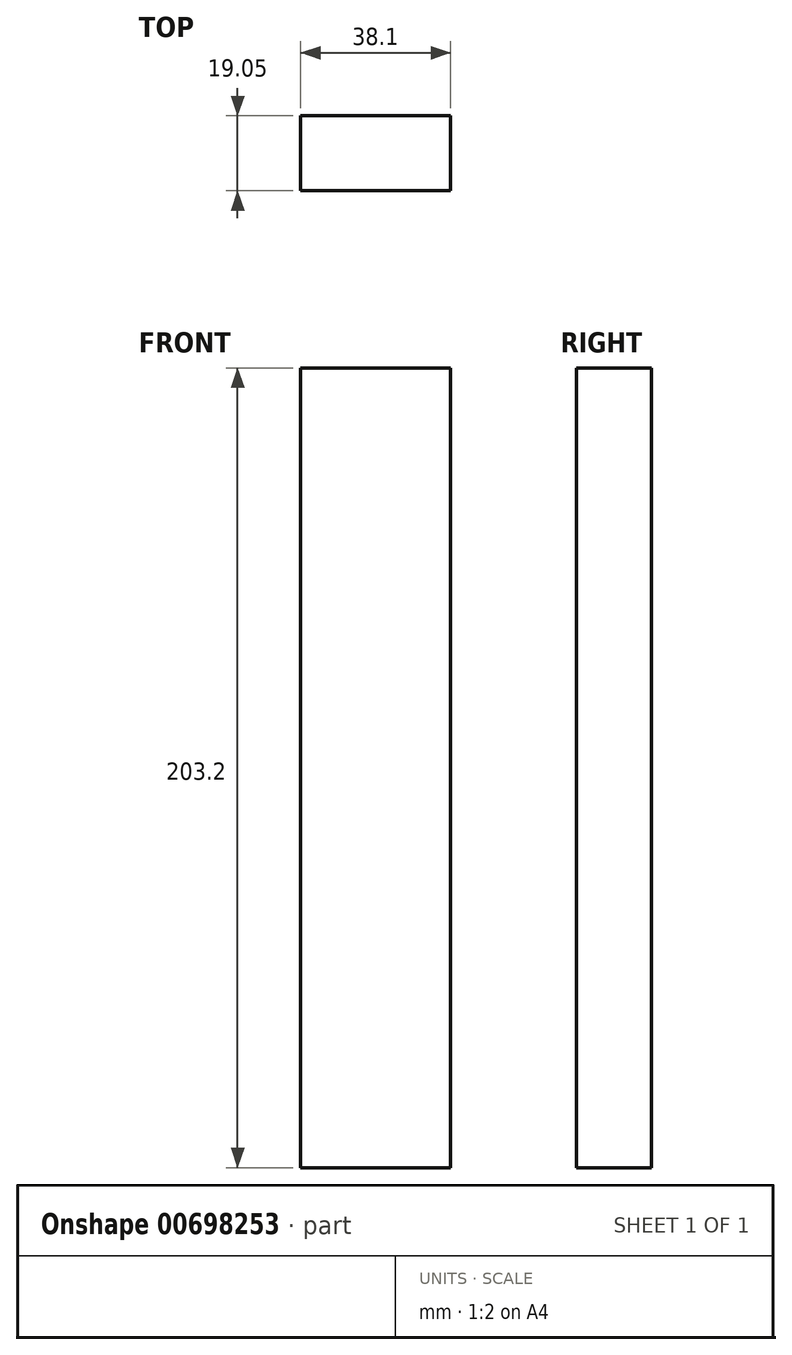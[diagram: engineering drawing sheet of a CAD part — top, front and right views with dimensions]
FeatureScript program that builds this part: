
annotation { "Feature Type Name" : "Feature", "Feature Type Description" : "" }
export const myFeature = defineFeature(function(context is Context, id is Id, definition is map)
    precondition{}
    {
        {
            var Q0;
            Q0=qCreatedBy(makeId("Front.planeOp"),FACE);
            var sketch = newSketch(context, id + "F0", { "sketchPlane" : qUnion([Q0])});
            skLineSegment(sketch, "E0.bottom", {"start": v(-37.95, 16.92) * mm, "end": v(0.15, 16.92) * mm});
            skLineSegment(sketch, "E0.top", {"start": v(-37.95, 220.12) * mm, "end": v(0.15, 220.12) * mm});
            skLineSegment(sketch, "E0.left", {"start": v(-37.95, 16.92) * mm, "end": v(-37.95, 220.12) * mm});
            skLineSegment(sketch, "E0.right", {"start": v(0.15, 16.92) * mm, "end": v(0.15, 220.12) * mm});
            skSolve(sketch);
        }
        {
            var Q0;
            Q0 = qSketchRegion(id + "F0", true);
            extrude(context, id + "F1", {"entities" : qUnion([Q0]), "depth" : 19.05 * mm, "offsetDistance" : 25.4 * mm});
        }
    });
